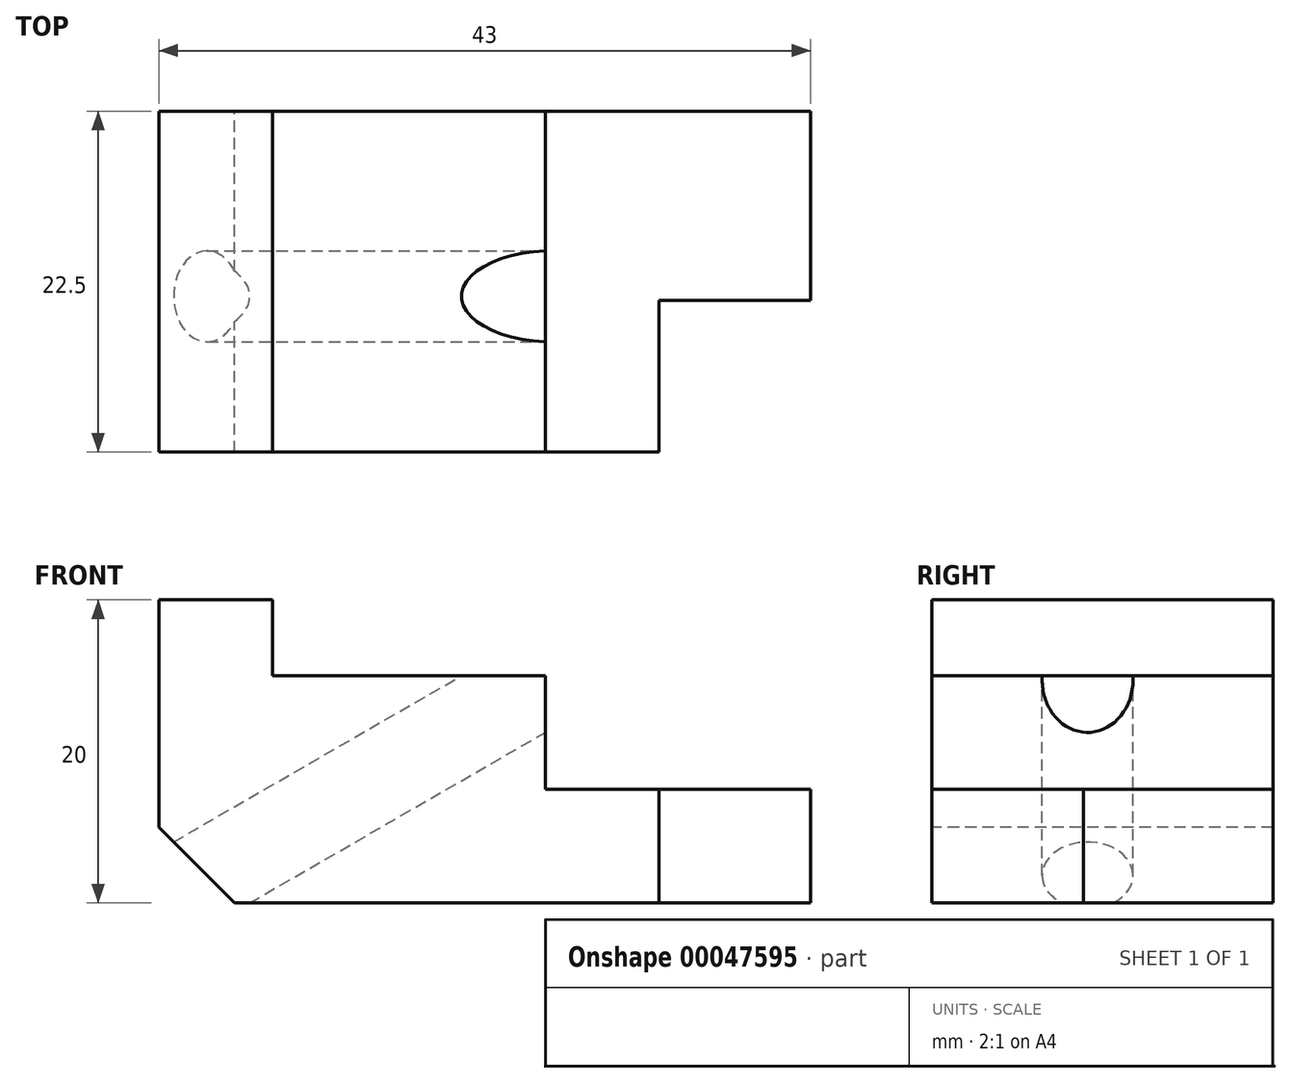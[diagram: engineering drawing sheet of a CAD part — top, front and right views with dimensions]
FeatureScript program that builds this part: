
annotation { "Feature Type Name" : "Feature", "Feature Type Description" : "" }
export const myFeature = defineFeature(function(context is Context, id is Id, definition is map)
    precondition{}
    {
        {
            var Q0;
            Q0=qCreatedBy(makeId("Front.planeOp"),FACE);
            var sketch = newSketch(context, id + "F0", { "sketchPlane" : qUnion([Q0])});
            skLineSegment(sketch, "E0", {"start": v(0, 0) * mm, "end": v(0, 20) * mm});
            skLineSegment(sketch, "E1", {"start": v(0, 20) * mm, "end": v(7.5, 20) * mm});
            skLineSegment(sketch, "E2", {"start": v(7.5, 20) * mm, "end": v(7.5, 15) * mm});
            skLineSegment(sketch, "E3", {"start": v(7.5, 15) * mm, "end": v(25.5, 15) * mm});
            skLineSegment(sketch, "E4", {"start": v(25.5, 15) * mm, "end": v(25.5, 7.5) * mm});
            skLineSegment(sketch, "E5", {"start": v(25.5, 7.5) * mm, "end": v(43, 7.5) * mm});
            skLineSegment(sketch, "E6", {"start": v(43, 7.5) * mm, "end": v(43, 0) * mm});
            skLineSegment(sketch, "E7", {"start": v(43, 0) * mm, "end": v(0, 0) * mm});
            skSolve(sketch);
        }
        {
            var Q0;
            Q0=makeQuery(id+"F0.imprint","IMPRINT",FACE,{"disambiguationData":[TD([[makeQuery(id+"F0.imprint","IMPRINT",EDGE,{"derivedFrom":sQuery(id+"F0.wireOp",EDGE,"E0")}),-1.0]])]});
            extrude(context, id + "F1", {"entities" : qUnion([Q0]), "oppositeDirection" : true, "depth" : 22.5 * mm});
        }
        {
            var Q0;
            Q0=makeQuery(id+"F1.opExtrude","SWEPT_FACE",FACE,{"disambiguationData":[OSD([sQuery(id+"F0.wireOp",EDGE,"E5")])]});
            var sketch = newSketch(context, id + "F2", { "sketchPlane" : qUnion([Q0])});
            skLineSegment(sketch, "E8.bottom", {"start": v(43, 0) * mm, "end": v(33, 0) * mm});
            skLineSegment(sketch, "E8.top", {"start": v(43, 10) * mm, "end": v(33, 10) * mm});
            skLineSegment(sketch, "E8.left", {"start": v(43, 0) * mm, "end": v(43, 10) * mm});
            skLineSegment(sketch, "E8.right", {"start": v(33, 0) * mm, "end": v(33, 10) * mm});
            skSolve(sketch);
        }
        {
            var Q0;
            Q0=makeQuery(id+"F2.imprint","IMPRINT",FACE,{"disambiguationData":[TD([[makeQuery(id+"F2.imprint","IMPRINT",EDGE,{"derivedFrom":sQuery(id+"F2.wireOp",EDGE,"E8.bottom")}),1.0]])]});
            extrude(context, id + "F3", {"entities" : qUnion([Q0]), "operationType" : NewBodyOperationType.REMOVE, "endBound" : BoundingType.UP_TO_NEXT, "oppositeDirection" : true, "depth" : 25 * mm});
        }
        {
            var Q0;
            Q0=makeQuery(id+"F1.opExtrude","SWEPT_EDGE",EDGE,{"disambiguationData":[OSD([sQuery(id+"F0.wireOp",EDGE,"E0"),sQuery(id+"F0.wireOp",EDGE,"E7")])]});
            chamfer(context, id + "F4", {"entities" : qUnion([Q0]), "width" : 5 * mm, "tangentPropagation" : true});
        }
        {
            var Q0;
            Q0=makeQuery(id+"F1.opExtrude","SWEPT_EDGE",EDGE,{"disambiguationData":[OSD([sQuery(id+"F0.wireOp",EDGE,"E3"),sQuery(id+"F0.wireOp",EDGE,"E4")])]});
            cPlane(context, id + "F5", {"entities" : qUnion([Q0]), "cplaneType" : CPlaneType.LINE_ANGLE, "offset" : 150 * mm, "angle" : 120 * degree, "width" : 150 * mm, "height" : 150 * mm});
        }
        {
            var Q0;
            Q0=qCreatedBy(id+"F5.planeOp",FACE);
            var sketch = newSketch(context, id + "F6", { "sketchPlane" : qUnion([Q0])});
            skCircle(sketch, "E9", {"center": v(10.28, 0) * mm, "radius": 3 * mm});
            skSolve(sketch);
        }
        {
            var Q0;
            Q0=makeQuery(id+"F6.imprint","IMPRINT",FACE,{"disambiguationData":[TD([[makeQuery(id+"F6.imprint","IMPRINT",EDGE,{"derivedFrom":sQuery(id+"F6.wireOp",EDGE,"E9")}),1.0]])]});
            extrude(context, id + "F7", {"entities" : qUnion([Q0]), "operationType" : NewBodyOperationType.REMOVE, "endBound" : BoundingType.THROUGH_ALL, "oppositeDirection" : true, "depth" : 25 * mm});
        }
    });
